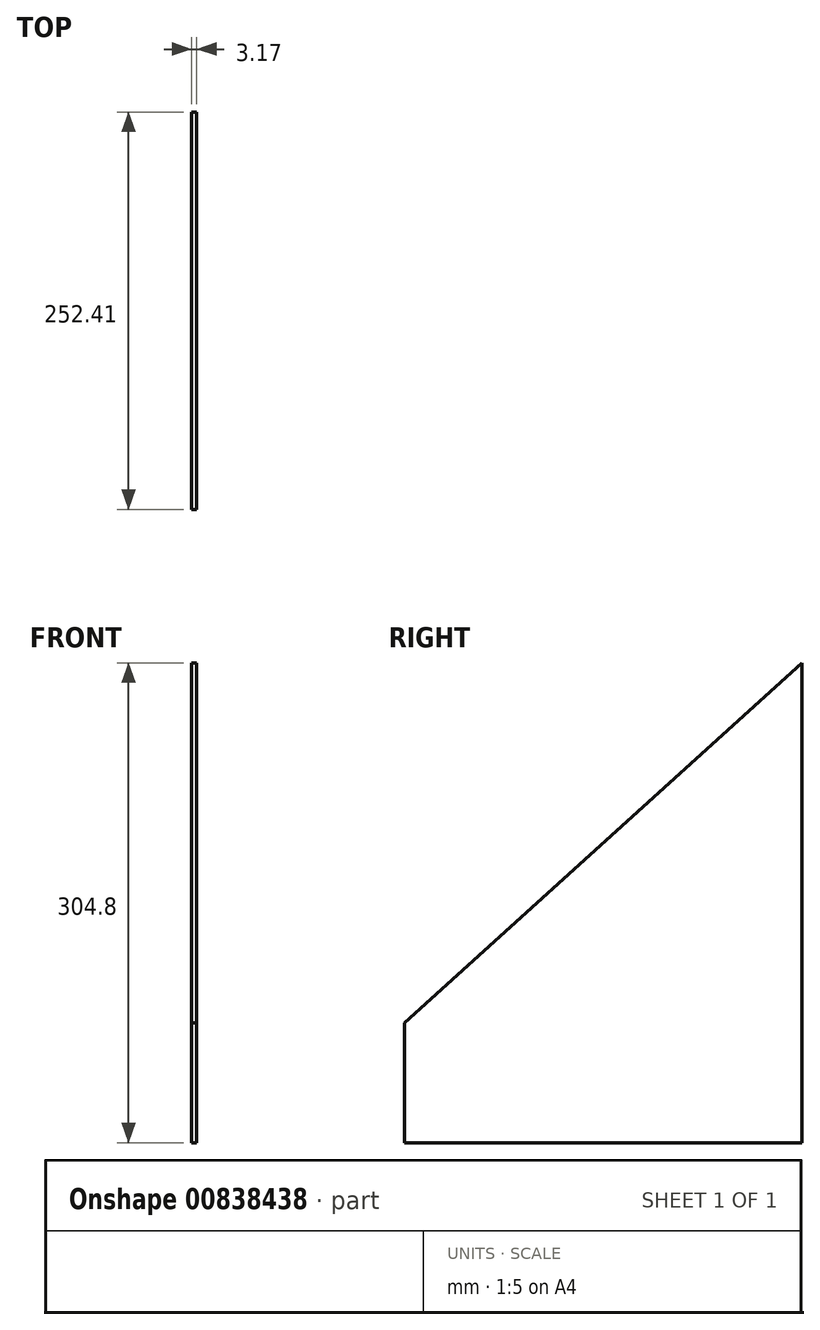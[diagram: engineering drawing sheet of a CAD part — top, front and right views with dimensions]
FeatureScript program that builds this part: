
annotation { "Feature Type Name" : "Feature", "Feature Type Description" : "" }
export const myFeature = defineFeature(function(context is Context, id is Id, definition is map)
    precondition{}
    {
        {
            var Q0;
            Q0=qCreatedBy(makeId("Right.planeOp"),FACE);
            var sketch = newSketch(context, id + "F0", { "sketchPlane" : qUnion([Q0])});
            skLineSegment(sketch, "E0", {"start": v(0, 0) * mm, "end": v(252.41, 0) * mm});
            skLineSegment(sketch, "E1", {"start": v(252.41, 0) * mm, "end": v(252.41, 304.8) * mm});
            skLineSegment(sketch, "E2", {"start": v(0, 0) * mm, "end": v(0, 76.2) * mm});
            skLineSegment(sketch, "E3", {"start": v(0, 76.2) * mm, "end": v(252.41, 304.8) * mm});
            skSolve(sketch);
        }
        {
            var Q0;
            Q0=makeQuery(id+"F0.imprint","IMPRINT",FACE,{"disambiguationData":[TD([[makeQuery(id+"F0.imprint","IMPRINT",EDGE,{"derivedFrom":sQuery(id+"F0.wireOp",EDGE,"E0")}),1.0]])]});
            extrude(context, id + "F1", {"entities" : qUnion([Q0]), "depth" : 3.17 * mm, "offsetDistance" : 25.4 * mm});
        }
    });
